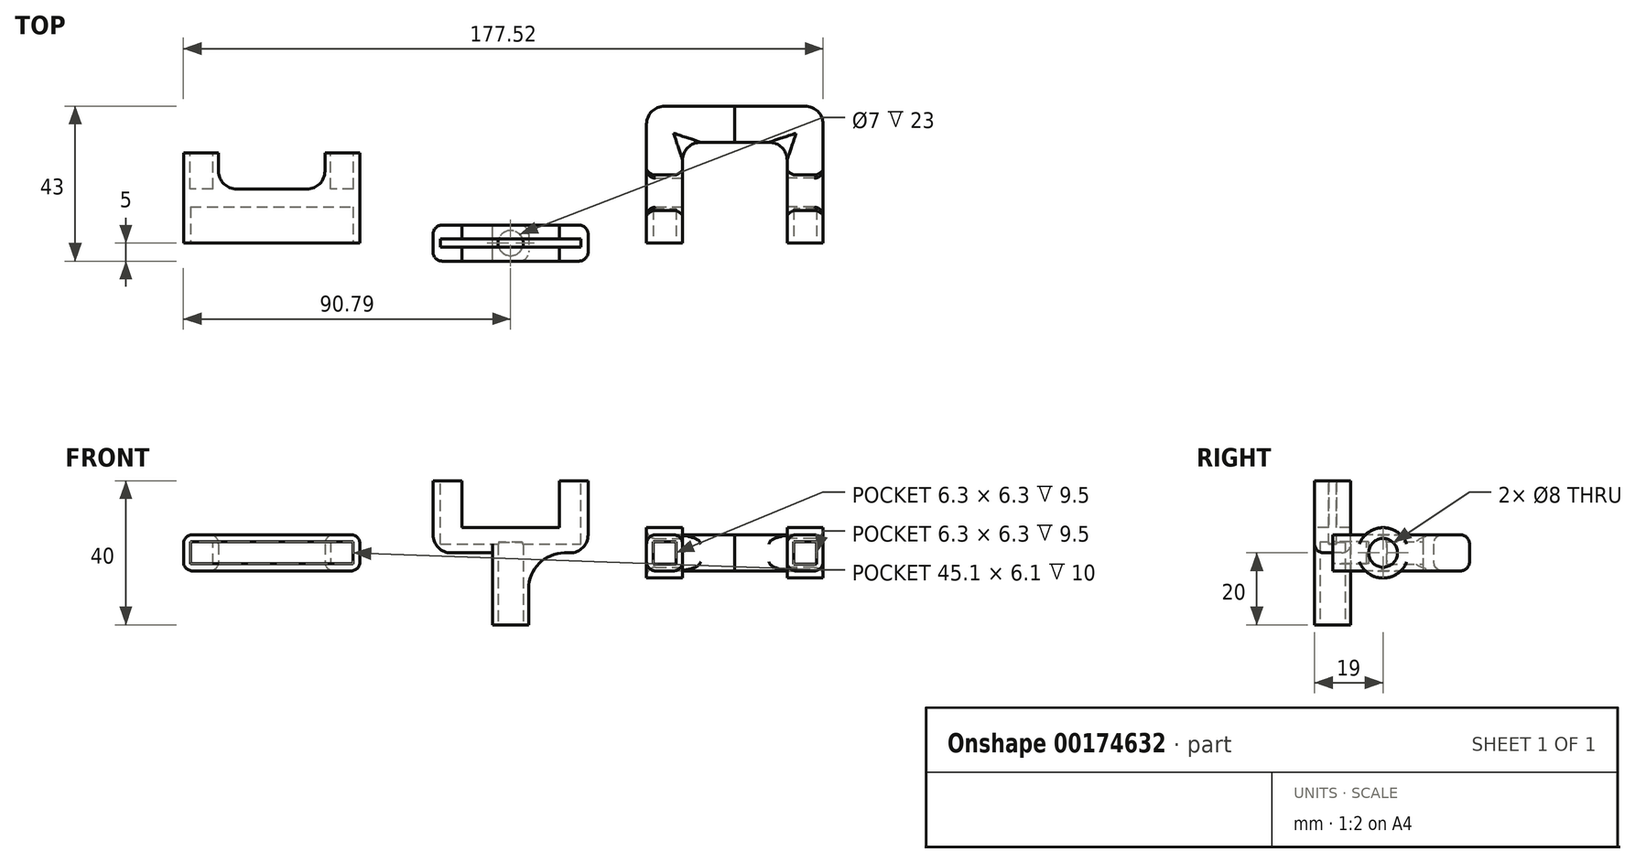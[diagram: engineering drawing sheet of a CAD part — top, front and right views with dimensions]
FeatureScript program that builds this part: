
annotation { "Feature Type Name" : "Feature", "Feature Type Description" : "" }
export const myFeature = defineFeature(function(context is Context, id is Id, definition is map)
    precondition{}
    {
        {
            var Q0;
            Q0=qCreatedBy(makeId("Top.planeOp"),FACE);
            var sketch = newSketch(context, id + "F0", { "sketchPlane" : qUnion([Q0])});
            skLineSegment(sketch, "E0.bottom", {"start": v(21.5, 5) * mm, "end": v(-21.5, 5) * mm});
            skLineSegment(sketch, "E0.top", {"start": v(21.5, -5) * mm, "end": v(-21.5, -5) * mm});
            skLineSegment(sketch, "E0.left", {"start": v(21.5, 5) * mm, "end": v(21.5, -5) * mm});
            skLineSegment(sketch, "E0.right", {"start": v(-21.5, 5) * mm, "end": v(-21.5, -5) * mm});
            skPoint(sketch, "E0.middle", {"position": v(0, 0) * mm});
            skSolve(sketch);
        }
        {
            var Q0;
            Q0=qSketchRegion(id+"F0",true);
            extrude(context, id + "F1", {"entities" : qUnion([Q0]), "depth" : 7 * mm});
        }
        {
            var Q0;
            Q0=makeQuery(id+"F1.opExtrude","CAP_FACE",FACE,{"disambiguationData":[OSD([sQuery(id+"F0.wireOp",EDGE,"E0.bottom"),sQuery(id+"F0.wireOp",EDGE,"E0.top"),sQuery(id+"F0.wireOp",EDGE,"E0.left"),sQuery(id+"F0.wireOp",EDGE,"E0.right")])],"isStart":false});
            var sketch = newSketch(context, id + "F2", { "sketchPlane" : qUnion([Q0])});
            skLineSegment(sketch, "E1.bottom", {"start": v(-21.5, 5) * mm, "end": v(-13.5, 5) * mm});
            skLineSegment(sketch, "E1.top", {"start": v(-21.5, -5) * mm, "end": v(-13.5, -5) * mm});
            skLineSegment(sketch, "E1.left", {"start": v(-21.5, 5) * mm, "end": v(-21.5, -5) * mm});
            skLineSegment(sketch, "E1.right", {"start": v(-13.5, 5) * mm, "end": v(-13.5, -5) * mm});
            skLineSegment(sketch, "E2.bottom", {"start": v(21.5, 5) * mm, "end": v(13.5, 5) * mm});
            skLineSegment(sketch, "E2.top", {"start": v(21.5, -5) * mm, "end": v(13.5, -5) * mm});
            skLineSegment(sketch, "E2.left", {"start": v(21.5, 5) * mm, "end": v(21.5, -5) * mm});
            skLineSegment(sketch, "E2.right", {"start": v(13.5, 5) * mm, "end": v(13.5, -5) * mm});
            skSolve(sketch);
        }
        {
            var Q0;
            Q0=makeQuery(id+"F2.imprint","IMPRINT",FACE,{"disambiguationData":[TD([[makeQuery(id+"F2.imprint","IMPRINT",EDGE,{"derivedFrom":sQuery(id+"F2.wireOp",EDGE,"E1.bottom")}),1.0]])]});
            var Q1;
            Q1=makeQuery(id+"F2.imprint","IMPRINT",FACE,{"disambiguationData":[TD([[makeQuery(id+"F2.imprint","IMPRINT",EDGE,{"derivedFrom":sQuery(id+"F2.wireOp",EDGE,"E2.bottom")}),1.0]])]});
            extrude(context, id + "F3", {"entities" : qUnion([Q0, Q1]), "operationType" : NewBodyOperationType.ADD, "depth" : 13 * mm});
        }
        {
            var Q0;
            Q0=makeQuery(id+"F1.opExtrude","CAP_FACE",FACE,{"disambiguationData":[OSD([sQuery(id+"F0.wireOp",EDGE,"E0.bottom"),sQuery(id+"F0.wireOp",EDGE,"E0.top"),sQuery(id+"F0.wireOp",EDGE,"E0.left"),sQuery(id+"F0.wireOp",EDGE,"E0.right")])],"isStart":true});
            var sketch = newSketch(context, id + "F4", { "sketchPlane" : qUnion([Q0])});
            skLineSegment(sketch, "E3.bottom", {"start": v(-5, 5) * mm, "end": v(5, 5) * mm});
            skLineSegment(sketch, "E3.top", {"start": v(-5, -5) * mm, "end": v(5, -5) * mm});
            skLineSegment(sketch, "E3.left", {"start": v(-5, 5) * mm, "end": v(-5, -5) * mm});
            skLineSegment(sketch, "E3.right", {"start": v(5, 5) * mm, "end": v(5, -5) * mm});
            skPoint(sketch, "E3.middle", {"position": v(0, 0) * mm});
            skSolve(sketch);
        }
        {
            var Q0;
            Q0=makeQuery(id+"F4.imprint","IMPRINT",FACE,{"disambiguationData":[TD([[makeQuery(id+"F4.imprint","IMPRINT",EDGE,{"derivedFrom":sQuery(id+"F4.wireOp",EDGE,"E3.bottom")}),1.0]])]});
            extrude(context, id + "F5", {"entities" : qUnion([Q0]), "operationType" : NewBodyOperationType.ADD, "depth" : 20 * mm});
        }
        {
            var Q0;
            Q0=makeQuery(id+"F5.opExtrude","CAP_FACE",FACE,{"disambiguationData":[OSD([sQuery(id+"F4.wireOp",EDGE,"E3.bottom"),sQuery(id+"F4.wireOp",EDGE,"E3.top"),sQuery(id+"F4.wireOp",EDGE,"E3.left"),sQuery(id+"F4.wireOp",EDGE,"E3.right")])],"isStart":false});
            var sketch = newSketch(context, id + "F6", { "sketchPlane" : qUnion([Q0])});
            skCircle(sketch, "E4", {"center": v(0, 0) * mm, "radius": 3.5 * mm});
            skSolve(sketch);
        }
        {
            var Q0;
            Q0=qSketchRegion(id+"F6",true);
            extrude(context, id + "F7", {"entities" : qUnion([Q0]), "operationType" : NewBodyOperationType.REMOVE, "oppositeDirection" : true, "depth" : 23 * mm});
        }
        {
            var Q0;
            Q0=makeQuery(id+"F5.boolean.opBoolean","MERGE",FACE,{"derivedFrom":[makeQuery(id+"F3.boolean.opBoolean","MERGE",FACE,{"derivedFrom":[makeQuery(id+"F1.opExtrude","SWEPT_FACE",FACE,{"disambiguationData":[OSD([sQuery(id+"F0.wireOp",EDGE,"E0.top")])]}),makeQuery(id+"F3.opExtrude","SWEPT_FACE",FACE,{"disambiguationData":[OSD([sQuery(id+"F2.wireOp",EDGE,"E1.top")])]}),makeQuery(id+"F3.opExtrude","SWEPT_FACE",FACE,{"disambiguationData":[OSD([sQuery(id+"F2.wireOp",EDGE,"E2.top")])]})]}),makeQuery(id+"F5.opExtrude","SWEPT_FACE",FACE,{"disambiguationData":[OSD([sQuery(id+"F4.wireOp",EDGE,"E3.bottom")])]})]});
            var sketch = newSketch(context, id + "F8", { "sketchPlane" : qUnion([Q0])});
            skLineSegment(sketch, "E5", {"start": v(-5, 0) * mm, "end": v(-15, 0) * mm});
            skLineSegment(sketch, "E6", {"start": v(-15, 0) * mm, "end": v(-5, 0) * mm});
            skLineSegment(sketch, "E7", {"start": v(-5, 0) * mm, "end": v(-5, -10) * mm});
            skArc(sketch, "E8", {"start": v(-5, -10) * mm, "mid": v(-7.93, -2.93) * mm, "end": v(-15, 0) * mm});
            skLineSegment(sketch, "E9", {"start": v(5, 0) * mm, "end": v(15, 0) * mm});
            skLineSegment(sketch, "E10", {"start": v(5, 0) * mm, "end": v(5, -10) * mm});
            skArc(sketch, "E11", {"start": v(15, 0) * mm, "mid": v(7.93, -2.93) * mm, "end": v(5, -10) * mm});
            skSolve(sketch);
        }
        {
            var Q0;
            Q0=makeQuery(id+"F8.imprint","IMPRINT",FACE,{"disambiguationData":[TD([[makeQuery(id+"F8.imprint","IMPRINT",EDGE,{"derivedFrom":sQuery(id+"F8.wireOp",EDGE,"E6")}),1.0]])]});
            var Q1;
            Q1=makeQuery(id+"F8.imprint","IMPRINT",FACE,{"disambiguationData":[TD([[makeQuery(id+"F8.imprint","IMPRINT",EDGE,{"derivedFrom":sQuery(id+"F8.wireOp",EDGE,"E9")}),1.0]])]});
            extrude(context, id + "F9", {"entities" : qUnion([Q0, Q1]), "operationType" : NewBodyOperationType.ADD, "oppositeDirection" : true, "depth" : 10 * mm});
        }
        {
            var Q0;
            Q0=makeQuery(id+"F3.opExtrude","CAP_FACE",FACE,{"disambiguationData":[OSD([sQuery(id+"F2.wireOp",EDGE,"E1.bottom"),sQuery(id+"F2.wireOp",EDGE,"E1.top"),sQuery(id+"F2.wireOp",EDGE,"E1.left"),sQuery(id+"F2.wireOp",EDGE,"E1.right")])],"isStart":false});
            var sketch = newSketch(context, id + "F10", { "sketchPlane" : qUnion([Q0])});
            skLineSegment(sketch, "E12.bottom", {"start": v(-19.5, 1.13) * mm, "end": v(19.5, 1.13) * mm});
            skLineSegment(sketch, "E12.top", {"start": v(-19.5, -1.13) * mm, "end": v(19.5, -1.13) * mm});
            skLineSegment(sketch, "E12.left", {"start": v(-19.5, 1.13) * mm, "end": v(-19.5, -1.13) * mm});
            skLineSegment(sketch, "E12.right", {"start": v(19.5, 1.13) * mm, "end": v(19.5, -1.13) * mm});
            skPoint(sketch, "E12.middle", {"position": v(0, 0) * mm});
            skSolve(sketch);
        }
        {
            var Q0;
            Q0=qSketchRegion(id+"F10",true);
            extrude(context, id + "F11", {"entities" : qUnion([Q0]), "oppositeDirection" : true, "depth" : 17.6 * mm});
        }
        {
            var Q0;
            Q0=makeQuery(id+"F11.opExtrude","SWEPT_BODY",BODY,{"disambiguationData":[OSD([sQuery(id+"F10.wireOp",EDGE,"E12.bottom"),sQuery(id+"F10.wireOp",EDGE,"E12.top"),sQuery(id+"F10.wireOp",EDGE,"E12.left"),sQuery(id+"F10.wireOp",EDGE,"E12.right")])]});
            var Q1;
            Q1=makeQuery(id+"F1.opExtrude","SWEPT_BODY",BODY,{"disambiguationData":[OSD([sQuery(id+"F0.wireOp",EDGE,"E0.bottom"),sQuery(id+"F0.wireOp",EDGE,"E0.top"),sQuery(id+"F0.wireOp",EDGE,"E0.left"),sQuery(id+"F0.wireOp",EDGE,"E0.right")])]});
            booleanBodies(context, id + "F12", {"operationType" : BooleanOperationType.SUBTRACTION, "tools" : qUnion([Q0]), "targets" : qUnion([Q1])});
        }
        {
            var Q0;
            Q0=makeQuery(id+"F1.opExtrude","CAP_EDGE",EDGE,{"disambiguationData":[OSD([sQuery(id+"F0.wireOp",EDGE,"E0.right")])],"isStart":true});
            fillet(context, id + "F13", {"entities" : qUnion([Q0]), "radius" : 5 * mm, "tangentPropagation" : true, "allowEdgeOverflow" : false});
        }
        {
            var Q0;
            Q0=makeQuery(id+"F1.opExtrude","CAP_EDGE",EDGE,{"disambiguationData":[OSD([sQuery(id+"F0.wireOp",EDGE,"E0.left")])],"isStart":true});
            fillet(context, id + "F14", {"entities" : qUnion([Q0]), "radius" : 5 * mm, "tangentPropagation" : true, "allowEdgeOverflow" : false});
        }
        {
            var Q0;
            Q0=makeQuery(id+"F3.boolean.opBoolean","MERGE",EDGE,{"derivedFrom":[makeQuery(id+"F1.opExtrude","SWEPT_EDGE",EDGE,{"disambiguationData":[OSD([sQuery(id+"F0.wireOp",EDGE,"E0.bottom"),sQuery(id+"F0.wireOp",EDGE,"E0.right")])]}),makeQuery(id+"F3.opExtrude","SWEPT_EDGE",EDGE,{"disambiguationData":[OSD([sQuery(id+"F2.wireOp",EDGE,"E1.bottom"),sQuery(id+"F2.wireOp",EDGE,"E1.left")])]})]});
            var Q1;
            Q1=makeQuery(id+"F3.boolean.opBoolean","MERGE",EDGE,{"derivedFrom":[makeQuery(id+"F1.opExtrude","SWEPT_EDGE",EDGE,{"disambiguationData":[OSD([sQuery(id+"F0.wireOp",EDGE,"E0.top"),sQuery(id+"F0.wireOp",EDGE,"E0.right")])]}),makeQuery(id+"F3.opExtrude","SWEPT_EDGE",EDGE,{"disambiguationData":[OSD([sQuery(id+"F2.wireOp",EDGE,"E1.top"),sQuery(id+"F2.wireOp",EDGE,"E1.left")])]})]});
            var Q2;
            Q2=makeQuery(id+"F9.opExtrude","CAP_EDGE",EDGE,{"disambiguationData":[OSD([sQuery(id+"F8.wireOp",EDGE,"E11")])],"isStart":false});
            var Q3;
            Q3=makeQuery(id+"F3.boolean.opBoolean","MERGE",EDGE,{"derivedFrom":[makeQuery(id+"F1.opExtrude","SWEPT_EDGE",EDGE,{"disambiguationData":[OSD([sQuery(id+"F0.wireOp",EDGE,"E0.top"),sQuery(id+"F0.wireOp",EDGE,"E0.left")])]}),makeQuery(id+"F3.opExtrude","SWEPT_EDGE",EDGE,{"disambiguationData":[OSD([sQuery(id+"F2.wireOp",EDGE,"E2.top"),sQuery(id+"F2.wireOp",EDGE,"E2.left")])]})]});
            var Q4;
            {var subQ0=sQuery(id+"F2.wireOp",EDGE,"E1.right");var subQ1=sQuery(id+"F0.wireOp",EDGE,"E0.bottom");Q4=makeQuery(id+"F12.opBoolean","SPLIT",EDGE,{"disambiguationData":[TD([makeQuery(id+"F1.opExtrude","SWEPT_FACE",FACE,{"disambiguationData":[OSD([subQ1])]})])],"derivedFrom":makeQuery(id+"F3.opExtrude","CAP_EDGE",EDGE,{"disambiguationData":[OSD([subQ0])],"isStart":true})});}
            var Q5;
            {var subQ0=sQuery(id+"F2.wireOp",EDGE,"E1.right");var subQ1=sQuery(id+"F0.wireOp",EDGE,"E0.top");Q5=makeQuery(id+"F12.opBoolean","SPLIT",EDGE,{"disambiguationData":[TD([makeQuery(id+"F1.opExtrude","SWEPT_FACE",FACE,{"disambiguationData":[OSD([subQ1])]})])],"derivedFrom":makeQuery(id+"F3.opExtrude","CAP_EDGE",EDGE,{"disambiguationData":[OSD([subQ0])],"isStart":true})});}
            var Q6;
            {var subQ0=sQuery(id+"F0.wireOp",EDGE,"E0.bottom");var subQ1=sQuery(id+"F2.wireOp",EDGE,"E2.right");Q6=makeQuery(id+"F12.opBoolean","SPLIT",EDGE,{"disambiguationData":[TD([makeQuery(id+"F1.opExtrude","SWEPT_FACE",FACE,{"disambiguationData":[OSD([subQ0])]})])],"derivedFrom":makeQuery(id+"F3.opExtrude","CAP_EDGE",EDGE,{"disambiguationData":[OSD([subQ1])],"isStart":true})});}
            var Q7;
            {var subQ0=sQuery(id+"F0.wireOp",EDGE,"E0.top");var subQ1=sQuery(id+"F2.wireOp",EDGE,"E2.right");Q7=makeQuery(id+"F12.opBoolean","SPLIT",EDGE,{"disambiguationData":[TD([makeQuery(id+"F1.opExtrude","SWEPT_FACE",FACE,{"disambiguationData":[OSD([subQ0])]})])],"derivedFrom":makeQuery(id+"F3.opExtrude","CAP_EDGE",EDGE,{"disambiguationData":[OSD([subQ1])],"isStart":true})});}
            fillet(context, id + "F15", {"entities" : qUnion([Q0, Q1, Q2, Q3, Q4, Q5, Q6, Q7]), "radius" : 2.5 * mm, "tangentPropagation" : true, "allowEdgeOverflow" : false});
        }
        {
            var Q0;
            Q0=qCreatedBy(makeId("Front.planeOp"),FACE);
            var sketch = newSketch(context, id + "F16", { "sketchPlane" : qUnion([Q0])});
            skLineSegment(sketch, "E13.bottom", {"start": v(-90.79, 5) * mm, "end": v(-41.79, 5) * mm});
            skLineSegment(sketch, "E13.top", {"start": v(-90.79, -5) * mm, "end": v(-41.79, -5) * mm});
            skLineSegment(sketch, "E13.left", {"start": v(-90.79, 5) * mm, "end": v(-90.79, -5) * mm});
            skLineSegment(sketch, "E13.right", {"start": v(-41.79, 5) * mm, "end": v(-41.79, -5) * mm});
            skPoint(sketch, "E14", {"position": v(-66.29, 0) * mm});
            skSolve(sketch);
        }
        {
            var Q0;
            Q0=qSketchRegion(id+"F16",true);
            extrude(context, id + "F17", {"entities" : qUnion([Q0]), "oppositeDirection" : true, "depth" : 25 * mm});
        }
        {
            var Q0;
            Q0=makeQuery(id+"F17.opExtrude","CAP_FACE",FACE,{"disambiguationData":[OSD([sQuery(id+"F16.wireOp",EDGE,"E13.bottom"),sQuery(id+"F16.wireOp",EDGE,"E13.top"),sQuery(id+"F16.wireOp",EDGE,"E13.left"),sQuery(id+"F16.wireOp",EDGE,"E13.right")])],"isStart":true});
            var sketch = newSketch(context, id + "F18", { "sketchPlane" : qUnion([Q0])});
            skLineSegment(sketch, "E15", {"start": v(-66.29, 5) * mm, "end": v(-66.29, -5) * mm, "construction": true});
            skLineSegment(sketch, "E16.bottom", {"start": v(-88.84, 3.05) * mm, "end": v(-43.74, 3.05) * mm});
            skLineSegment(sketch, "E16.top", {"start": v(-88.84, -3.05) * mm, "end": v(-43.74, -3.05) * mm});
            skLineSegment(sketch, "E16.left", {"start": v(-88.84, 3.05) * mm, "end": v(-88.84, -3.05) * mm});
            skLineSegment(sketch, "E16.right", {"start": v(-43.74, 3.05) * mm, "end": v(-43.74, -3.05) * mm});
            skPoint(sketch, "E16.middle", {"position": v(-66.29, 0) * mm});
            skSolve(sketch);
        }
        {
            var Q0;
            Q0=qSketchRegion(id+"F18",true);
            extrude(context, id + "F19", {"entities" : qUnion([Q0]), "operationType" : NewBodyOperationType.REMOVE, "oppositeDirection" : true, "depth" : 10 * mm});
        }
        {
            var Q0;
            Q0=makeQuery(id+"F17.opExtrude","CAP_FACE",FACE,{"disambiguationData":[OSD([sQuery(id+"F16.wireOp",EDGE,"E13.bottom"),sQuery(id+"F16.wireOp",EDGE,"E13.top"),sQuery(id+"F16.wireOp",EDGE,"E13.left"),sQuery(id+"F16.wireOp",EDGE,"E13.right")])],"isStart":false});
            var sketch = newSketch(context, id + "F20", { "sketchPlane" : qUnion([Q0])});
            skLineSegment(sketch, "E17", {"start": v(41.79, 0) * mm, "end": v(90.79, 0) * mm, "construction": true});
            skLineSegment(sketch, "E18", {"start": v(41.79, 0) * mm, "end": v(46.79, 0) * mm, "construction": true});
            skLineSegment(sketch, "E19.bottom", {"start": v(43.64, 3.15) * mm, "end": v(49.94, 3.15) * mm});
            skLineSegment(sketch, "E19.top", {"start": v(43.64, -3.15) * mm, "end": v(49.94, -3.15) * mm});
            skLineSegment(sketch, "E19.left", {"start": v(43.64, 3.15) * mm, "end": v(43.64, -3.15) * mm});
            skLineSegment(sketch, "E19.right", {"start": v(49.94, 3.15) * mm, "end": v(49.94, -3.15) * mm});
            skPoint(sketch, "E19.middle", {"position": v(46.79, 0) * mm});
            skLineSegment(sketch, "E20", {"start": v(90.79, 0) * mm, "end": v(85.79, 0) * mm, "construction": true});
            skLineSegment(sketch, "E21.bottom", {"start": v(82.64, -3.15) * mm, "end": v(88.94, -3.15) * mm});
            skLineSegment(sketch, "E21.top", {"start": v(82.64, 3.15) * mm, "end": v(88.94, 3.15) * mm});
            skLineSegment(sketch, "E21.left", {"start": v(82.64, -3.15) * mm, "end": v(82.64, 3.15) * mm});
            skLineSegment(sketch, "E21.right", {"start": v(88.94, -3.15) * mm, "end": v(88.94, 3.15) * mm});
            skPoint(sketch, "E21.middle", {"position": v(85.79, 0) * mm});
            skSolve(sketch);
        }
        {
            var Q0;
            Q0=qSketchRegion(id+"F20",true);
            extrude(context, id + "F21", {"entities" : qUnion([Q0]), "operationType" : NewBodyOperationType.REMOVE, "oppositeDirection" : true, "depth" : 10 * mm});
        }
        {
            var Q0;
            Q0=makeQuery(id+"F17.opExtrude","SWEPT_EDGE",EDGE,{"disambiguationData":[OSD([sQuery(id+"F16.wireOp",EDGE,"E13.bottom"),sQuery(id+"F16.wireOp",EDGE,"E13.left")])]});
            var Q1;
            Q1=makeQuery(id+"F17.opExtrude","SWEPT_EDGE",EDGE,{"disambiguationData":[OSD([sQuery(id+"F16.wireOp",EDGE,"E13.bottom"),sQuery(id+"F16.wireOp",EDGE,"E13.right")])]});
            var Q2;
            Q2=makeQuery(id+"F17.opExtrude","SWEPT_EDGE",EDGE,{"disambiguationData":[OSD([sQuery(id+"F16.wireOp",EDGE,"E13.top"),sQuery(id+"F16.wireOp",EDGE,"E13.right")])]});
            var Q3;
            Q3=makeQuery(id+"F17.opExtrude","SWEPT_EDGE",EDGE,{"disambiguationData":[OSD([sQuery(id+"F16.wireOp",EDGE,"E13.top"),sQuery(id+"F16.wireOp",EDGE,"E13.left")])]});
            fillet(context, id + "F22", {"entities" : qUnion([Q0, Q1, Q2, Q3]), "radius" : 2.5 * mm, "tangentPropagation" : true, "allowEdgeOverflow" : false});
        }
        {
            var Q0;
            Q0=makeQuery(id+"F17.opExtrude","CAP_FACE",FACE,{"disambiguationData":[OSD([sQuery(id+"F16.wireOp",EDGE,"E13.bottom"),sQuery(id+"F16.wireOp",EDGE,"E13.top"),sQuery(id+"F16.wireOp",EDGE,"E13.left"),sQuery(id+"F16.wireOp",EDGE,"E13.right")])],"isStart":false});
            var sketch = newSketch(context, id + "F23", { "sketchPlane" : qUnion([Q0])});
            skLineSegment(sketch, "E22", {"start": v(41.79, 0) * mm, "end": v(90.79, 0) * mm, "construction": true});
            skLineSegment(sketch, "E23.bottom", {"start": v(51.54, 7.07) * mm, "end": v(81.04, 7.07) * mm});
            skLineSegment(sketch, "E23.top", {"start": v(51.54, -7.07) * mm, "end": v(81.04, -7.07) * mm});
            skLineSegment(sketch, "E23.left", {"start": v(51.54, 7.07) * mm, "end": v(51.54, -7.07) * mm});
            skLineSegment(sketch, "E23.right", {"start": v(81.04, 7.07) * mm, "end": v(81.04, -7.07) * mm});
            skPoint(sketch, "E23.middle", {"position": v(66.29, 0) * mm});
            skSolve(sketch);
        }
        {
            var Q0;
            Q0=qSketchRegion(id+"F23",true);
            extrude(context, id + "F24", {"entities" : qUnion([Q0]), "operationType" : NewBodyOperationType.REMOVE, "oppositeDirection" : true, "depth" : 10 * mm});
        }
        {
            var Q0;
            Q0=makeQuery(id+"F24.boolean.opBoolean","COPY",EDGE,{"derivedFrom":makeQuery(id+"F24.opExtrude","CAP_EDGE",EDGE,{"disambiguationData":[OSD([sQuery(id+"F23.wireOp",EDGE,"E23.left")])],"isStart":false})});
            var Q1;
            Q1=makeQuery(id+"F24.boolean.opBoolean","COPY",EDGE,{"derivedFrom":makeQuery(id+"F24.opExtrude","CAP_EDGE",EDGE,{"disambiguationData":[OSD([sQuery(id+"F23.wireOp",EDGE,"E23.right")])],"isStart":false})});
            fillet(context, id + "F25", {"entities" : qUnion([Q0, Q1]), "radius" : 5 * mm, "tangentPropagation" : true, "allowEdgeOverflow" : false});
        }
        {
            var Q0;
            Q0=makeQuery(id+"F24.boolean.opBoolean","INTERSECT",EDGE,{"derivedFrom":[makeQuery(id+"F17.opExtrude","SWEPT_FACE",FACE,{"disambiguationData":[OSD([sQuery(id+"F16.wireOp",EDGE,"E13.bottom")])]}),makeQuery(id+"F24.opExtrude","SWEPT_FACE",FACE,{"disambiguationData":[OSD([sQuery(id+"F23.wireOp",EDGE,"E23.left")])]})]});
            var Q1;
            Q1=makeQuery(id+"F24.boolean.opBoolean","INTERSECT",EDGE,{"derivedFrom":[makeQuery(id+"F17.opExtrude","SWEPT_FACE",FACE,{"disambiguationData":[OSD([sQuery(id+"F16.wireOp",EDGE,"E13.top")])]}),makeQuery(id+"F24.opExtrude","CAP_FACE",FACE,{"disambiguationData":[OSD([sQuery(id+"F23.wireOp",EDGE,"E23.bottom"),sQuery(id+"F23.wireOp",EDGE,"E23.top"),sQuery(id+"F23.wireOp",EDGE,"E23.left"),sQuery(id+"F23.wireOp",EDGE,"E23.right")])],"isStart":false})]});
            fillet(context, id + "F26", {"entities" : qUnion([Q0, Q1]), "radius" : 2.5 * mm, "tangentPropagation" : true, "allowEdgeOverflow" : false});
        }
        {
            var Q0;
            Q0=qCreatedBy(makeId("Top.planeOp"),FACE);
            var sketch = newSketch(context, id + "F27", { "sketchPlane" : qUnion([Q0])});
            skLineSegment(sketch, "E24.bottom", {"start": v(37.73, 0) * mm, "end": v(47.73, 0) * mm});
            skLineSegment(sketch, "E24.top", {"start": v(37.73, 38) * mm, "end": v(62.23, 38) * mm});
            skLineSegment(sketch, "E24.left", {"start": v(37.73, 0) * mm, "end": v(37.73, 38) * mm});
            skLineSegment(sketch, "E24.right", {"start": v(62.23, 28) * mm, "end": v(62.23, 38) * mm});
            skLineSegment(sketch, "E25.top", {"start": v(62.23, 28) * mm, "end": v(47.73, 28) * mm});
            skLineSegment(sketch, "E25.right", {"start": v(47.73, 0) * mm, "end": v(47.73, 28) * mm});
            skPoint(sketch, "E26.orphan", {"position": v(62.23, 0) * mm});
            skLineSegment(sketch, "E27", {"start": v(62.23, 0) * mm, "end": v(62.23, 45.65) * mm, "construction": true});
            skLineSegment(sketch, "E28", {"start": v(32.97, 14) * mm, "end": v(53.85, 14) * mm, "construction": true});
            skLineSegment(sketch, "E29", {"start": v(35.58, 10) * mm, "end": v(51.63, 10) * mm, "construction": true});
            skLineSegment(sketch, "E30", {"start": v(35.58, 18) * mm, "end": v(51.63, 18) * mm, "construction": true});
            skSolve(sketch);
        }
        {
            var Q0;
            Q0=qSketchRegion(id+"F27",true);
            extrude(context, id + "F28", {"entities" : qUnion([Q0]), "depth" : 5 * mm, "hasSecondDirection" : true, "secondDirectionOppositeDirection" : true, "secondDirectionDepth" : 5 * mm});
        }
        {
            var Q0;
            Q0=makeQuery(id+"F28.opExtrude","SWEPT_FACE",FACE,{"disambiguationData":[OSD([sQuery(id+"F27.wireOp",EDGE,"E25.right")])]});
            var sketch = newSketch(context, id + "F29", { "sketchPlane" : qUnion([Q0])});
            skLineSegment(sketch, "E31", {"start": v(0, 0) * mm, "end": v(14, 0) * mm, "construction": true});
            skCircle(sketch, "E32", {"center": v(14, 0) * mm, "radius": 7 * mm});
            skSolve(sketch);
        }
        {
            var Q0;
            Q0=qSketchRegion(id+"F29",true);
            extrude(context, id + "F30", {"entities" : qUnion([Q0]), "operationType" : NewBodyOperationType.ADD, "oppositeDirection" : true, "depth" : 10 * mm});
        }
        {
            var Q0;
            Q0=makeQuery(id+"F28.opExtrude","SWEPT_FACE",FACE,{"disambiguationData":[OSD([sQuery(id+"F27.wireOp",EDGE,"E25.right")])]});
            var sketch = newSketch(context, id + "F31", { "sketchPlane" : qUnion([Q0])});
            skLineSegment(sketch, "E33", {"start": v(0, 0) * mm, "end": v(14, 0) * mm, "construction": true});
            skPoint(sketch, "E33.endSnap0", {"position": v(0, 0) * mm});
            skCircle(sketch, "E34", {"center": v(14, 0) * mm, "radius": 4 * mm});
            skSolve(sketch);
        }
        {
            var Q0;
            Q0=qSketchRegion(id+"F31",true);
            extrude(context, id + "F32", {"entities" : qUnion([Q0]), "operationType" : NewBodyOperationType.REMOVE, "oppositeDirection" : true, "depth" : 17.3 * mm});
        }
        {
            var Q0;
            Q0=makeQuery(id+"F28.opExtrude","SWEPT_FACE",FACE,{"disambiguationData":[OSD([sQuery(id+"F27.wireOp",EDGE,"E24.bottom")])]});
            var sketch = newSketch(context, id + "F33", { "sketchPlane" : qUnion([Q0])});
            skLineSegment(sketch, "E35", {"start": v(37.73, 0) * mm, "end": v(47.73, 0) * mm, "construction": true});
            skLineSegment(sketch, "E36.bottom", {"start": v(39.58, -3.15) * mm, "end": v(45.88, -3.15) * mm});
            skLineSegment(sketch, "E36.top", {"start": v(39.58, 3.15) * mm, "end": v(45.88, 3.15) * mm});
            skLineSegment(sketch, "E36.left", {"start": v(39.58, -3.15) * mm, "end": v(39.58, 3.15) * mm});
            skLineSegment(sketch, "E36.right", {"start": v(45.88, -3.15) * mm, "end": v(45.88, 3.15) * mm});
            skPoint(sketch, "E36.middle", {"position": v(42.73, 0) * mm});
            skSolve(sketch);
        }
        {
            var Q0;
            Q0=qSketchRegion(id+"F33",true);
            extrude(context, id + "F34", {"entities" : qUnion([Q0]), "operationType" : NewBodyOperationType.REMOVE, "oppositeDirection" : true, "depth" : 9.5 * mm});
        }
        {
            var Q0;
            Q0=makeQuery(id+"F32.boolean.opBoolean","COPY",EDGE,{"derivedFrom":makeQuery(id+"F32.opExtrude","CAP_EDGE",EDGE,{"disambiguationData":[OSD([sQuery(id+"F31.wireOp",EDGE,"E34")])],"isStart":true})});
            var Q1;
            Q1=makeQuery(id+"F32.boolean.opBoolean","INTERSECT",EDGE,{"derivedFrom":[makeQuery(id+"F30.boolean.opBoolean","MERGE",FACE,{"derivedFrom":[makeQuery(id+"F28.opExtrude","SWEPT_FACE",FACE,{"disambiguationData":[OSD([sQuery(id+"F27.wireOp",EDGE,"E24.left")])]}),makeQuery(id+"F30.opExtrude","CAP_FACE",FACE,{"disambiguationData":[OSD([sQuery(id+"F29.wireOp",EDGE,"E32")])],"isStart":false})]}),makeQuery(id+"F32.opExtrude","SWEPT_FACE",FACE,{"disambiguationData":[OSD([sQuery(id+"F31.wireOp",EDGE,"E34")])]})]});
            var Q2;
            {var subQ0=sQuery(id+"F27.wireOp",EDGE,"E25.right");var subQ2=sQuery(id+"F27.wireOp",EDGE,"E24.bottom");Q2=makeQuery(id+"F30.boolean.opBoolean","SPLIT",EDGE,{"disambiguationData":[TD([makeQuery(id+"F28.opExtrude","SWEPT_FACE",FACE,{"disambiguationData":[OSD([subQ2])]})])],"derivedFrom":makeQuery(id+"F28.opExtrude","CAP_EDGE",EDGE,{"disambiguationData":[OSD([subQ0])],"isStart":false})});}
            var Q3;
            {var subQ0=sQuery(id+"F27.wireOp",EDGE,"E25.right");var subQ2=sQuery(id+"F27.wireOp",EDGE,"E24.bottom");Q3=makeQuery(id+"F30.boolean.opBoolean","SPLIT",EDGE,{"disambiguationData":[TD([makeQuery(id+"F28.opExtrude","SWEPT_FACE",FACE,{"disambiguationData":[OSD([subQ2])]})])],"derivedFrom":makeQuery(id+"F28.opExtrude","CAP_EDGE",EDGE,{"disambiguationData":[OSD([subQ0])],"isStart":true})});}
            var Q4;
            {var subQ0=sQuery(id+"F27.wireOp",EDGE,"E25.right");var subQ1=sQuery(id+"F27.wireOp",EDGE,"E25.top");Q4=makeQuery(id+"F30.boolean.opBoolean","SPLIT",EDGE,{"disambiguationData":[TD([makeQuery(id+"F28.opExtrude","SWEPT_FACE",FACE,{"disambiguationData":[OSD([subQ1])]})])],"derivedFrom":makeQuery(id+"F28.opExtrude","CAP_EDGE",EDGE,{"disambiguationData":[OSD([subQ0])],"isStart":false})});}
            var Q5;
            {var subQ0=sQuery(id+"F27.wireOp",EDGE,"E25.right");var subQ1=sQuery(id+"F27.wireOp",EDGE,"E25.top");Q5=makeQuery(id+"F30.boolean.opBoolean","SPLIT",EDGE,{"disambiguationData":[TD([makeQuery(id+"F28.opExtrude","SWEPT_FACE",FACE,{"disambiguationData":[OSD([subQ1])]})])],"derivedFrom":makeQuery(id+"F28.opExtrude","CAP_EDGE",EDGE,{"disambiguationData":[OSD([subQ0])],"isStart":true})});}
            var Q6;
            {var subQ0=sQuery(id+"F27.wireOp",EDGE,"E24.left");var subQ2=sQuery(id+"F27.wireOp",EDGE,"E24.bottom");Q6=makeQuery(id+"F30.boolean.opBoolean","SPLIT",EDGE,{"disambiguationData":[TD([makeQuery(id+"F28.opExtrude","SWEPT_FACE",FACE,{"disambiguationData":[OSD([subQ2])]})])],"derivedFrom":makeQuery(id+"F28.opExtrude","CAP_EDGE",EDGE,{"disambiguationData":[OSD([subQ0])],"isStart":false})});}
            var Q7;
            {var subQ0=sQuery(id+"F27.wireOp",EDGE,"E24.left");var subQ2=sQuery(id+"F27.wireOp",EDGE,"E24.top");Q7=makeQuery(id+"F30.boolean.opBoolean","SPLIT",EDGE,{"disambiguationData":[TD([makeQuery(id+"F28.opExtrude","SWEPT_FACE",FACE,{"disambiguationData":[OSD([subQ2])]})])],"derivedFrom":makeQuery(id+"F28.opExtrude","CAP_EDGE",EDGE,{"disambiguationData":[OSD([subQ0])],"isStart":false})});}
            var Q8;
            Q8=makeQuery(id+"F28.opExtrude","CAP_EDGE",EDGE,{"disambiguationData":[OSD([sQuery(id+"F27.wireOp",EDGE,"E25.top")])],"isStart":false});
            var Q9;
            Q9=makeQuery(id+"F28.opExtrude","CAP_EDGE",EDGE,{"disambiguationData":[OSD([sQuery(id+"F27.wireOp",EDGE,"E25.top")])],"isStart":true});
            var Q10;
            Q10=makeQuery(id+"F28.opExtrude","CAP_EDGE",EDGE,{"disambiguationData":[OSD([sQuery(id+"F27.wireOp",EDGE,"E24.top")])],"isStart":false});
            var Q11;
            Q11=makeQuery(id+"F28.opExtrude","CAP_EDGE",EDGE,{"disambiguationData":[OSD([sQuery(id+"F27.wireOp",EDGE,"E24.top")])],"isStart":true});
            var Q12;
            {var subQ0=sQuery(id+"F27.wireOp",EDGE,"E24.left");var subQ2=sQuery(id+"F27.wireOp",EDGE,"E24.top");Q12=makeQuery(id+"F30.boolean.opBoolean","SPLIT",EDGE,{"disambiguationData":[TD([makeQuery(id+"F28.opExtrude","SWEPT_FACE",FACE,{"disambiguationData":[OSD([subQ2])]})])],"derivedFrom":makeQuery(id+"F28.opExtrude","CAP_EDGE",EDGE,{"disambiguationData":[OSD([subQ0])],"isStart":true})});}
            var Q13;
            {var subQ0=sQuery(id+"F27.wireOp",EDGE,"E24.left");var subQ2=sQuery(id+"F27.wireOp",EDGE,"E24.bottom");Q13=makeQuery(id+"F30.boolean.opBoolean","SPLIT",EDGE,{"disambiguationData":[TD([makeQuery(id+"F28.opExtrude","SWEPT_FACE",FACE,{"disambiguationData":[OSD([subQ2])]})])],"derivedFrom":makeQuery(id+"F28.opExtrude","CAP_EDGE",EDGE,{"disambiguationData":[OSD([subQ0])],"isStart":true})});}
            fillet(context, id + "F35", {"entities" : qUnion([Q0, Q1, Q2, Q3, Q4, Q5, Q6, Q7, Q8, Q9, Q10, Q11, Q12, Q13]), "radius" : 2.5 * mm, "tangentPropagation" : true, "allowEdgeOverflow" : false});
        }
        {
            var Q0;
            Q0=makeQuery(id+"F28.opExtrude","SWEPT_EDGE",EDGE,{"disambiguationData":[OSD([sQuery(id+"F27.wireOp",EDGE,"E25.top"),sQuery(id+"F27.wireOp",EDGE,"E25.right")])]});
            var Q1;
            Q1=makeQuery(id+"F28.opExtrude","SWEPT_EDGE",EDGE,{"disambiguationData":[OSD([sQuery(id+"F27.wireOp",EDGE,"E24.top"),sQuery(id+"F27.wireOp",EDGE,"E24.left")])]});
            fillet(context, id + "F36", {"entities" : qUnion([Q0, Q1]), "radius" : 5 * mm, "tangentPropagation" : true, "allowEdgeOverflow" : false});
        }
        {
            var Q0;
            Q0=makeQuery(id+"F28.opExtrude","SWEPT_BODY",BODY,{"disambiguationData":[OSD([sQuery(id+"F27.wireOp",EDGE,"E24.bottom"),sQuery(id+"F27.wireOp",EDGE,"E24.top"),sQuery(id+"F27.wireOp",EDGE,"E24.left"),sQuery(id+"F27.wireOp",EDGE,"E24.right"),sQuery(id+"F27.wireOp",EDGE,"E25.top"),sQuery(id+"F27.wireOp",EDGE,"E25.right")])]});
            var Q1;
            Q1=makeQuery(id+"F28.opExtrude","SWEPT_FACE",FACE,{"disambiguationData":[OSD([sQuery(id+"F27.wireOp",EDGE,"E24.right")])]});
            mirror(context, id + "F37", {"operationType" : NewBodyOperationType.ADD, "entities" : qUnion([Q0]), "mirrorPlane" : qUnion([Q1])});
        }
    });
